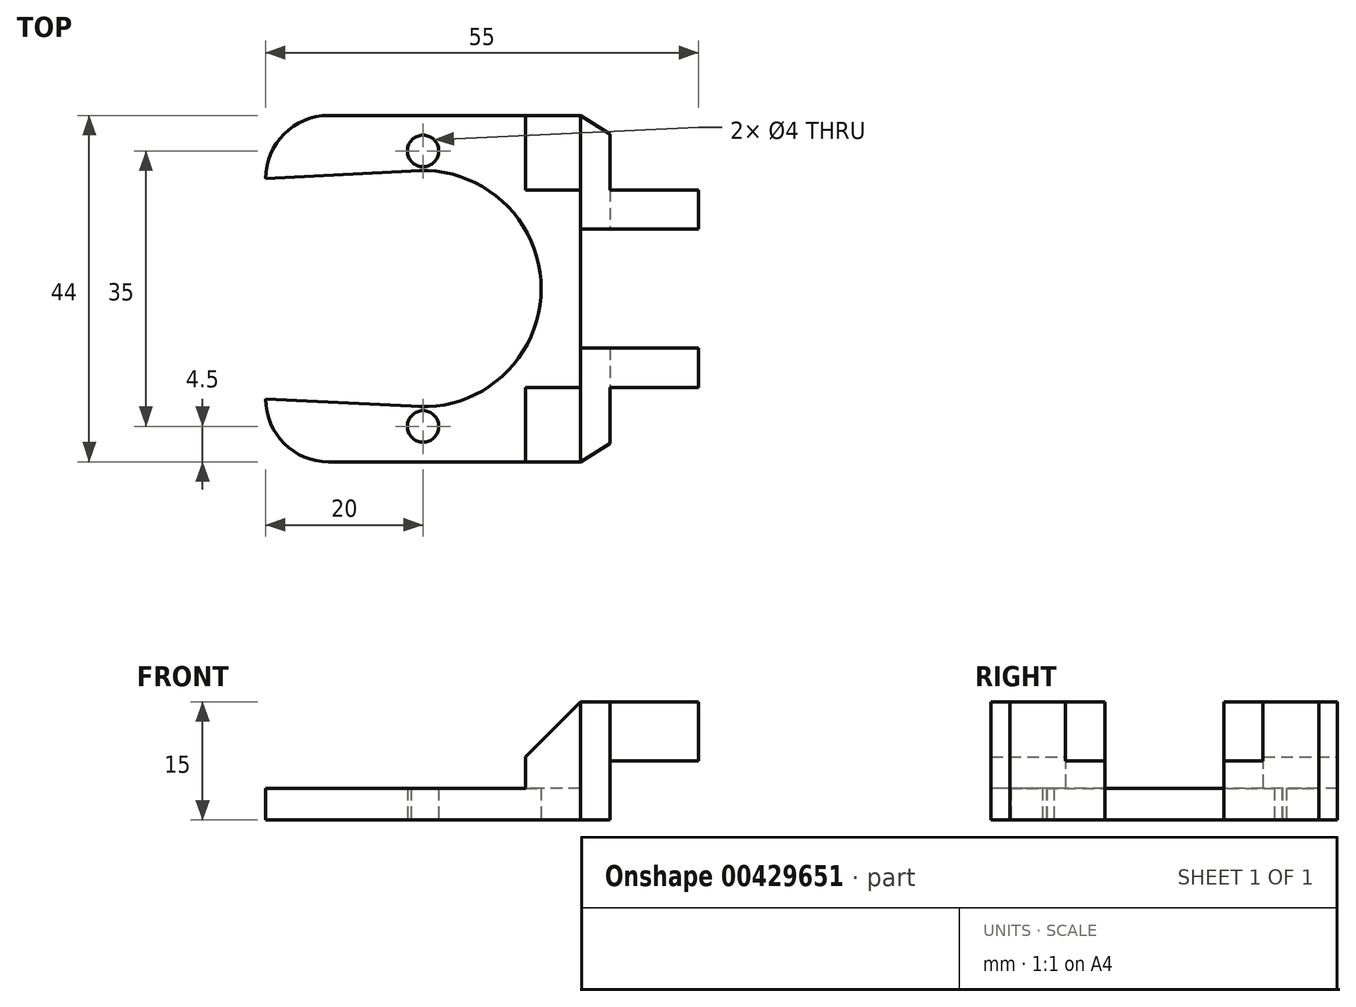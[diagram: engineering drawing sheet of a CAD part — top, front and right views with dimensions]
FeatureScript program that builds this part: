
annotation { "Feature Type Name" : "Feature", "Feature Type Description" : "" }
export const myFeature = defineFeature(function(context is Context, id is Id, definition is map)
    precondition{}
    {
        {
            var Q0;
            Q0=qCreatedBy(makeId("Top.planeOp"),FACE);
            var sketch = newSketch(context, id + "F0", { "sketchPlane" : qUnion([Q0])});
            skLineSegment(sketch, "E0.bottom", {"start": v(20, 22) * mm, "end": v(-12, 22) * mm});
            skLineSegment(sketch, "E0.top", {"start": v(20, -22) * mm, "end": v(-12, -22) * mm});
            skLineSegment(sketch, "E0.left", {"start": v(20, 22) * mm, "end": v(20, -22) * mm});
            skLineSegment(sketch, "E0.right", {"start": v(-20, 14) * mm, "end": v(-20, -14) * mm});
            skPoint(sketch, "E0.middle", {"position": v(0, 0) * mm});
            skPoint(sketch, "E1.visualSharp", {"position": v(-20, -22) * mm});
            skArc(sketch, "E1.filletArc", {"start": v(-20, -14) * mm, "mid": v(-17.66, -19.66) * mm, "end": v(-12, -22) * mm});
            skPoint(sketch, "E2.visualSharp", {"position": v(-20, 22) * mm});
            skArc(sketch, "E2.filletArc", {"start": v(-12, 22) * mm, "mid": v(-17.66, 19.66) * mm, "end": v(-20, 14) * mm});
            skCircle(sketch, "E3", {"center": v(0, 0) * mm, "radius": 15 * mm});
            skLineSegment(sketch, "E4", {"start": v(0, 0) * mm, "end": v(0, 17.5) * mm});
            skLineSegment(sketch, "E5", {"start": v(0, 0) * mm, "end": v(0, -17.5) * mm});
            skCircle(sketch, "E6", {"center": v(0, -17.5) * mm, "radius": 2 * mm});
            skCircle(sketch, "E7", {"center": v(0, 17.5) * mm, "radius": 2 * mm});
            skLineSegment(sketch, "E8", {"start": v(0, -15) * mm, "end": v(-20, -14) * mm});
            skLineSegment(sketch, "E9", {"start": v(0, 15) * mm, "end": v(-20, 14) * mm});
            skSolve(sketch);
        }
        {
            var Q0;
            Q0=makeQuery(id+"F0.imprint","IMPRINT",FACE,{"disambiguationData":[TD([[makeQuery(id+"F0.imprint","IMPRINT",EDGE,{"derivedFrom":sQuery(id+"F0.wireOp",EDGE,"E0.bottom")}),1.0]])]});
            extrude(context, id + "F1", {"entities" : qUnion([Q0]), "depth" : 4 * mm});
        }
        {
            var Q0;
            Q0=qCreatedBy(makeId("Top.planeOp"),FACE);
            var sketch = newSketch(context, id + "F2", { "sketchPlane" : qUnion([Q0])});
            skLineSegment(sketch, "E10", {"start": v(0, 0) * mm, "end": v(20, 0) * mm});
            skLineSegment(sketch, "E11", {"start": v(20, 0) * mm, "end": v(20, 7.55) * mm});
            skLineSegment(sketch, "E12", {"start": v(20, 0) * mm, "end": v(20, -7.55) * mm});
            skLineSegment(sketch, "E13", {"start": v(20, -7.55) * mm, "end": v(35, -7.55) * mm});
            skLineSegment(sketch, "E14", {"start": v(35, -7.55) * mm, "end": v(35, -12.55) * mm});
            skLineSegment(sketch, "E15", {"start": v(35, -12.55) * mm, "end": v(20, -12.55) * mm});
            skLineSegment(sketch, "E16", {"start": v(20, -12.55) * mm, "end": v(20, -7.55) * mm});
            skLineSegment(sketch, "E17", {"start": v(20, 7.55) * mm, "end": v(35, 7.55) * mm});
            skLineSegment(sketch, "E18", {"start": v(35, 7.55) * mm, "end": v(35, 12.55) * mm});
            skLineSegment(sketch, "E19", {"start": v(35, 12.55) * mm, "end": v(20, 12.55) * mm});
            skLineSegment(sketch, "E20", {"start": v(20, 12.55) * mm, "end": v(20, 22) * mm});
            skLineSegment(sketch, "E21", {"start": v(35, 12.55) * mm, "end": v(20, 22) * mm});
            skLineSegment(sketch, "E22", {"start": v(20, -12.55) * mm, "end": v(20, -22) * mm});
            skLineSegment(sketch, "E23", {"start": v(20, -22) * mm, "end": v(35, -12.55) * mm});
            skLineSegment(sketch, "E24", {"start": v(20, 12.55) * mm, "end": v(13, 12.55) * mm});
            skLineSegment(sketch, "E25", {"start": v(13, 12.55) * mm, "end": v(13, 22) * mm});
            skLineSegment(sketch, "E26", {"start": v(13, 22) * mm, "end": v(20, 22) * mm});
            skLineSegment(sketch, "E27", {"start": v(20, -22) * mm, "end": v(13, -22) * mm});
            skLineSegment(sketch, "E28", {"start": v(13, -22) * mm, "end": v(13, -12.55) * mm});
            skLineSegment(sketch, "E29", {"start": v(13, -12.55) * mm, "end": v(20, -12.55) * mm});
            skLineSegment(sketch, "E30", {"start": v(20, 7.55) * mm, "end": v(20, 12.55) * mm});
            skSolve(sketch);
        }
        {
            var Q0;
            Q0 = qSketchRegion(id + "F2", true);
            extrude(context, id + "F3", {"entities" : qUnion([Q0]), "operationType" : NewBodyOperationType.ADD, "depth" : 15 * mm});
        }
        {
            var Q0;
            Q0=makeQuery(id+"F3.opExtrude","CAP_EDGE",EDGE,{"disambiguationData":[OSD([sQuery(id+"F2.wireOp",EDGE,"E25")])],"isStart":false});
            var Q1;
            Q1=makeQuery(id+"F3.opExtrude","CAP_EDGE",EDGE,{"disambiguationData":[OSD([sQuery(id+"F2.wireOp",EDGE,"E28")])],"isStart":false});
            chamfer(context, id + "F4", {"entities" : qUnion([Q0, Q1]), "width" : 7 * mm, "tangentPropagation" : true});
        }
        {
            var Q0;
            Q0=makeQuery(id+"F3.opExtrude","CAP_FACE",FACE,{"disambiguationData":[OSD([sQuery(id+"F2.wireOp",EDGE,"E17"),sQuery(id+"F2.wireOp",EDGE,"E18"),sQuery(id+"F2.wireOp",EDGE,"E21"),sQuery(id+"F2.wireOp",EDGE,"E24"),sQuery(id+"F2.wireOp",EDGE,"E25"),sQuery(id+"F2.wireOp",EDGE,"E26"),sQuery(id+"F2.wireOp",EDGE,"E30")])],"isStart":false});
            var sketch = newSketch(context, id + "F5", { "sketchPlane" : qUnion([Q0])});
            skLineSegment(sketch, "E31", {"start": v(35, 12.55) * mm, "end": v(20, 12.55) * mm});
            skLineSegment(sketch, "E32", {"start": v(27.5, 12.55) * mm, "end": v(20, 12.55) * mm});
            skLineSegment(sketch, "E33", {"start": v(23.75, 12.55) * mm, "end": v(23.75, 19.64) * mm});
            skLineSegment(sketch, "E34", {"start": v(23.75, 19.64) * mm, "end": v(35, 12.55) * mm});
            skSolve(sketch);
        }
        {
            var Q0;
            {var subQ0=sQuery(id+"F5.wireOp",EDGE,"E31");Q0=makeQuery(id+"F5.imprint","IMPRINT",FACE,{"disambiguationData":[TD([[makeQuery(id+"F5.imprint","IMPRINT",EDGE,{"derivedFrom":subQ0}),-1.0]])]});}
            extrude(context, id + "F6", {"entities" : qUnion([Q0]), "operationType" : NewBodyOperationType.REMOVE, "oppositeDirection" : true, "depth" : 25 * mm});
        }
        {
            var Q0;
            Q0=makeQuery(id+"F3.opExtrude","CAP_FACE",FACE,{"disambiguationData":[OSD([sQuery(id+"F2.wireOp",EDGE,"E13"),sQuery(id+"F2.wireOp",EDGE,"E14"),sQuery(id+"F2.wireOp",EDGE,"E16"),sQuery(id+"F2.wireOp",EDGE,"E23"),sQuery(id+"F2.wireOp",EDGE,"E27"),sQuery(id+"F2.wireOp",EDGE,"E28"),sQuery(id+"F2.wireOp",EDGE,"E29")])],"isStart":false});
            var sketch = newSketch(context, id + "F7", { "sketchPlane" : qUnion([Q0])});
            skLineSegment(sketch, "E35", {"start": v(35, -12.55) * mm, "end": v(20, -12.55) * mm});
            skLineSegment(sketch, "E36", {"start": v(20, -12.55) * mm, "end": v(27.5, -12.55) * mm});
            skLineSegment(sketch, "E37", {"start": v(27.5, -12.55) * mm, "end": v(23.75, -12.55) * mm});
            skLineSegment(sketch, "E38", {"start": v(23.75, -12.55) * mm, "end": v(23.75, -19.64) * mm});
            skLineSegment(sketch, "E39", {"start": v(23.75, -19.64) * mm, "end": v(35, -12.55) * mm});
            skSolve(sketch);
        }
        {
            var Q0;
            Q0=makeQuery(id+"F7.imprint","IMPRINT",FACE,{"disambiguationData":[TD([[makeQuery(id+"F7.imprint","IMPRINT",EDGE,{"derivedFrom":sQuery(id+"F7.wireOp",EDGE,"E35")}),1.0]])]});
            extrude(context, id + "F8", {"entities" : qUnion([Q0]), "operationType" : NewBodyOperationType.REMOVE, "oppositeDirection" : true, "depth" : 25 * mm});
        }
        {
            var Q0;
            Q0=makeQuery(id+"F8.boolean.opBoolean","COPY",FACE,{"derivedFrom":makeQuery(id+"F8.opExtrude","SWEPT_FACE",FACE,{"disambiguationData":[OSD([sQuery(id+"F7.wireOp",EDGE,"E35"),sQuery(id+"F7.wireOp",EDGE,"E37")])]})});
            var sketch = newSketch(context, id + "F9", { "sketchPlane" : qUnion([Q0])});
            skLineSegment(sketch, "E40", {"start": v(29.38, 15) * mm, "end": v(29.38, 0) * mm});
            skLineSegment(sketch, "E41", {"start": v(35, 7.5) * mm, "end": v(23.75, 7.5) * mm});
            skPoint(sketch, "E42", {"position": v(29.38, 7.5) * mm});
            skCircle(sketch, "E43", {"center": v(29.38, 7.5) * mm, "radius": 1.75 * mm});
            skSolve(sketch);
        }
        {
            var Q0;
            {var subQ0=sQuery(id+"F9.wireOp",EDGE,"E41");var subQ1=sQuery(id+"F9.wireOp",EDGE,"E40");var subQ2=makeQuery(id+"F9.imprint","INTERSECT",VERTEX,{"derivedFrom":[subQ1,subQ0]});Q0=makeQuery(id+"F9.imprint","IMPRINT",FACE,{"disambiguationData":[TD([[makeQuery(id+"F9.imprint","IMPRINT",EDGE,{"disambiguationData":[TD([[subQ2,-1.0]])],"derivedFrom":subQ1}),1.0]])]});}
            var Q1;
            {var subQ0=sQuery(id+"F9.wireOp",EDGE,"E43");var subQ1=sQuery(id+"F9.wireOp",EDGE,"E40");var subQ2=makeQuery(id+"F9.imprint","INTERSECT",VERTEX,{"disambiguationData":[OD(0.0)],"derivedFrom":[subQ1,subQ0]});Q1=makeQuery(id+"F9.imprint","IMPRINT",FACE,{"disambiguationData":[TD([[makeQuery(id+"F9.imprint","IMPRINT",EDGE,{"disambiguationData":[TD([[subQ2,-1.0]])],"derivedFrom":subQ1}),1.0]])]});}
            var Q2;
            {var subQ0=sQuery(id+"F9.wireOp",EDGE,"E43");var subQ1=sQuery(id+"F9.wireOp",EDGE,"E40");var subQ2=makeQuery(id+"F9.imprint","INTERSECT",VERTEX,{"disambiguationData":[OD(0.0)],"derivedFrom":[subQ1,subQ0]});Q2=makeQuery(id+"F9.imprint","IMPRINT",FACE,{"disambiguationData":[TD([[makeQuery(id+"F9.imprint","IMPRINT",EDGE,{"disambiguationData":[TD([[subQ2,-1.0]])],"derivedFrom":subQ1}),-1.0]])]});}
            var Q3;
            {var subQ0=sQuery(id+"F9.wireOp",EDGE,"E41");var subQ1=sQuery(id+"F9.wireOp",EDGE,"E40");var subQ2=makeQuery(id+"F9.imprint","INTERSECT",VERTEX,{"derivedFrom":[subQ1,subQ0]});Q3=makeQuery(id+"F9.imprint","IMPRINT",FACE,{"disambiguationData":[TD([[makeQuery(id+"F9.imprint","IMPRINT",EDGE,{"disambiguationData":[TD([[subQ2,-1.0]])],"derivedFrom":subQ1}),-1.0]])]});}
            extrude(context, id + "F10", {"entities" : qUnion([Q0, Q1, Q2, Q3]), "operationType" : NewBodyOperationType.REMOVE, "oppositeDirection" : true, "depth" : 50 * mm});
        }
    });
